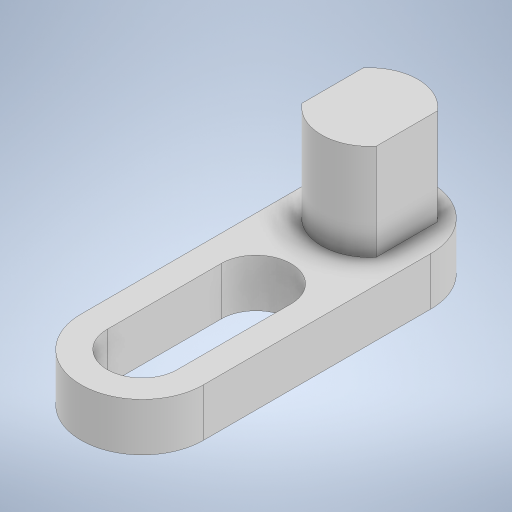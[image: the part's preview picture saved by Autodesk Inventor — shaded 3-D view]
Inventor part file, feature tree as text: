
AUTODESK INVENTOR PART (.ipt)
format: ipt  version: 2023 (Build 270158000, 158)  size: 239,616 bytes
history: native  units: mm
features: extrude x2, sketch x1
ambient origin geometry x8: Origin, YZ Plane, XZ Plane, XY Plane, X Axis, Y Axis, Z Axis, Center Point
bodies: Solido1 (feature_tree)
feature tree (3):
  sketch  "Schizzo1"
  extrude  "Estrusione1"  Depth=22.0mm
  extrude  "Estrusione2"  Depth=8.5mm
